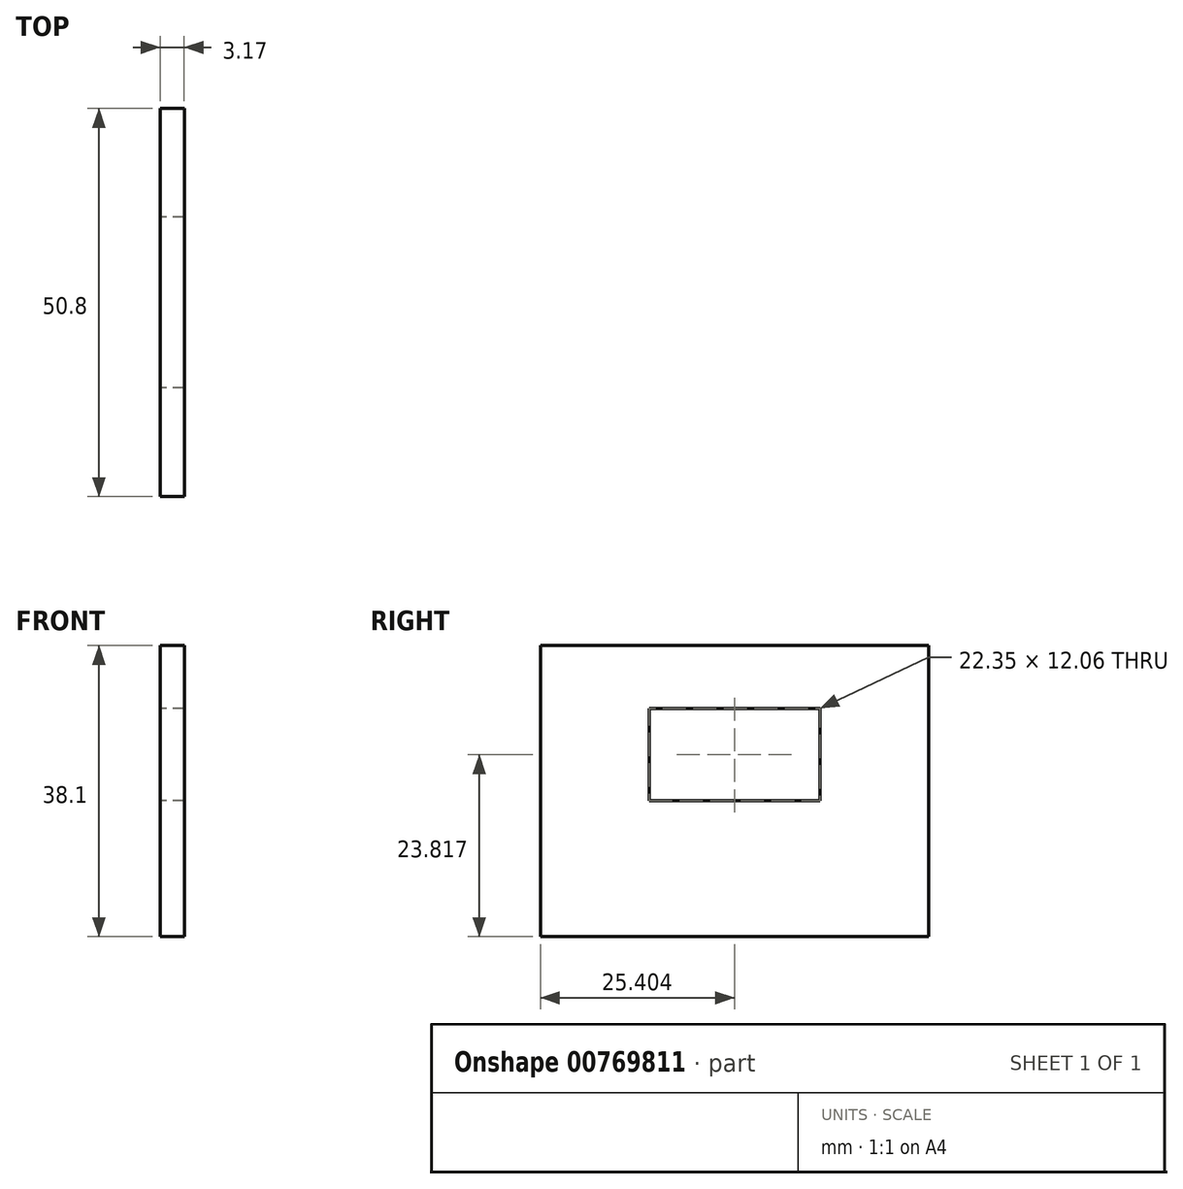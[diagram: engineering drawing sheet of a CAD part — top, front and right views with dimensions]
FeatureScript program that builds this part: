
annotation { "Feature Type Name" : "Feature", "Feature Type Description" : "" }
export const myFeature = defineFeature(function(context is Context, id is Id, definition is map)
    precondition{}
    {
        {
            var Q0;
            Q0=qCreatedBy(makeId("Right.planeOp"),FACE);
            var sketch = newSketch(context, id + "F0", { "sketchPlane" : qUnion([Q0])});
            skLineSegment(sketch, "E0.bottom", {"start": v(-37.84, 29.8) * mm, "end": v(12.96, 29.8) * mm});
            skLineSegment(sketch, "E0.top", {"start": v(-37.84, -8.3) * mm, "end": v(12.96, -8.3) * mm});
            skLineSegment(sketch, "E0.left", {"start": v(-37.84, 29.8) * mm, "end": v(-37.84, -8.3) * mm});
            skLineSegment(sketch, "E0.right", {"start": v(12.96, 29.8) * mm, "end": v(12.96, -8.3) * mm});
            skLineSegment(sketch, "E1.bottom", {"start": v(-1.26, 9.47) * mm, "end": v(-23.61, 9.47) * mm});
            skLineSegment(sketch, "E1.top", {"start": v(-1.26, 21.54) * mm, "end": v(-23.61, 21.54) * mm});
            skLineSegment(sketch, "E1.left", {"start": v(-1.26, 9.47) * mm, "end": v(-1.26, 21.54) * mm});
            skLineSegment(sketch, "E1.right", {"start": v(-23.61, 9.47) * mm, "end": v(-23.61, 21.54) * mm});
            skPoint(sketch, "E1.middle", {"position": v(-12.44, 15.5) * mm});
            skSolve(sketch);
        }
        {
            var Q0;
            Q0=makeQuery(id+"F0.imprint","IMPRINT",FACE,{"disambiguationData":[TD([[makeQuery(id+"F0.imprint","IMPRINT",EDGE,{"derivedFrom":sQuery(id+"F0.wireOp",EDGE,"E0.bottom")}),-1.0]])]});
            extrude(context, id + "F1", {"entities" : qUnion([Q0]), "depth" : 3.17 * mm, "offsetDistance" : 25.4 * mm});
        }
    });
